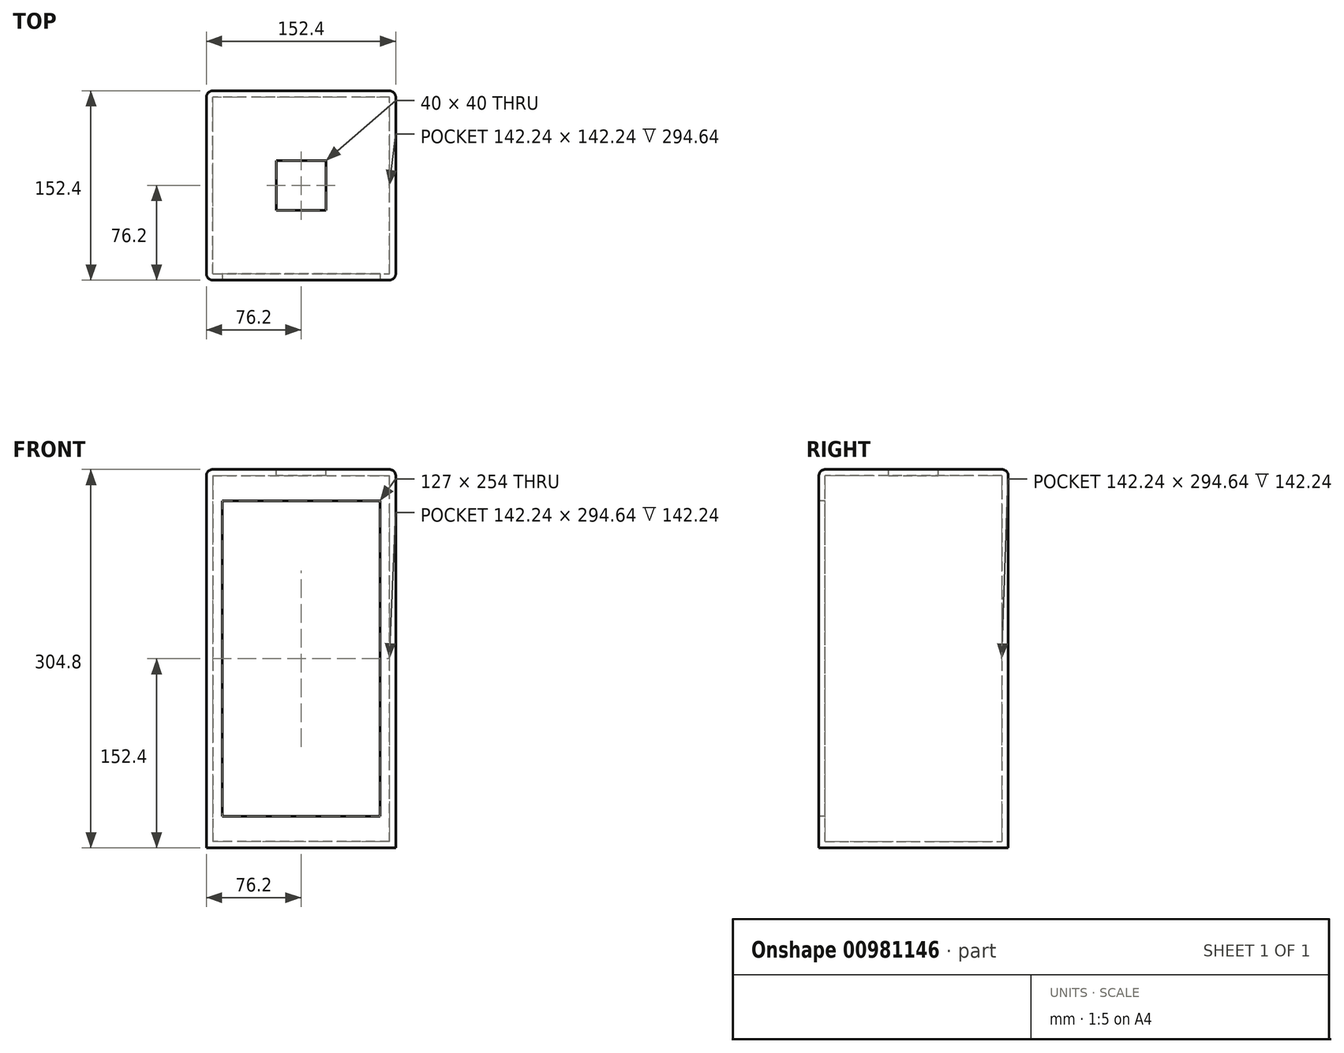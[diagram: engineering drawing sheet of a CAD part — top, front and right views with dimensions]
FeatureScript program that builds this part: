
annotation { "Feature Type Name" : "Feature", "Feature Type Description" : "" }
export const myFeature = defineFeature(function(context is Context, id is Id, definition is map)
    precondition{}
    {
        {
            var Q0;
            Q0=qCreatedBy(makeId("Front.planeOp"),FACE);
            var sketch = newSketch(context, id + "F0", { "sketchPlane" : qUnion([Q0])});
            skLineSegment(sketch, "E0.bottom", {"start": v(76.2, -152.4) * mm, "end": v(-76.2, -152.4) * mm});
            skLineSegment(sketch, "E0.top", {"start": v(76.2, 152.4) * mm, "end": v(-76.2, 152.4) * mm});
            skLineSegment(sketch, "E0.left", {"start": v(76.2, -152.4) * mm, "end": v(76.2, 152.4) * mm});
            skLineSegment(sketch, "E0.right", {"start": v(-76.2, -152.4) * mm, "end": v(-76.2, 152.4) * mm});
            skPoint(sketch, "E0.middle", {"position": v(0, 0) * mm});
            skSolve(sketch);
        }
        {
            var Q0;
            Q0 = qSketchRegion(id + "F0", true);
            extrude(context, id + "F1", {"entities" : qUnion([Q0]), "endBound" : BoundingType.SYMMETRIC, "depth" : 152.4 * mm, "offsetDistance" : 25.4 * mm});
        }
        {
            var Q0;
            Q0=makeQuery(id+"F1.opExtrude","CAP_EDGE",EDGE,{"disambiguationData":[OSD([sQuery(id+"F0.wireOp",EDGE,"E0.top")])],"isStart":false});
            var Q1;
            Q1=makeQuery(id+"F1.opExtrude","SWEPT_EDGE",EDGE,{"disambiguationData":[OSD([sQuery(id+"F0.wireOp",EDGE,"E0.top"),sQuery(id+"F0.wireOp",EDGE,"E0.left")])]});
            var Q2;
            Q2=makeQuery(id+"F1.opExtrude","CAP_EDGE",EDGE,{"disambiguationData":[OSD([sQuery(id+"F0.wireOp",EDGE,"E0.left")])],"isStart":false});
            var Q3;
            Q3=makeQuery(id+"F1.opExtrude","CAP_EDGE",EDGE,{"disambiguationData":[OSD([sQuery(id+"F0.wireOp",EDGE,"E0.left")])],"isStart":true});
            var Q4;
            Q4=makeQuery(id+"F1.opExtrude","CAP_EDGE",EDGE,{"disambiguationData":[OSD([sQuery(id+"F0.wireOp",EDGE,"E0.top")])],"isStart":true});
            var Q5;
            Q5=makeQuery(id+"F1.opExtrude","SWEPT_EDGE",EDGE,{"disambiguationData":[OSD([sQuery(id+"F0.wireOp",EDGE,"E0.top"),sQuery(id+"F0.wireOp",EDGE,"E0.right")])]});
            var Q6;
            Q6=makeQuery(id+"F1.opExtrude","CAP_EDGE",EDGE,{"disambiguationData":[OSD([sQuery(id+"F0.wireOp",EDGE,"E0.right")])],"isStart":false});
            var Q7;
            Q7=makeQuery(id+"F1.opExtrude","CAP_EDGE",EDGE,{"disambiguationData":[OSD([sQuery(id+"F0.wireOp",EDGE,"E0.right")])],"isStart":true});
            fillet(context, id + "F2", {"entities" : qUnion([Q0, Q1, Q2, Q3, Q4, Q5, Q6, Q7]), "radius" : 5.08 * mm, "tangentPropagation" : true, "allowEdgeOverflow" : false});
        }
        {
            var Q0;
            Q0=makeQuery(id+"F1.opExtrude","CAP_FACE",FACE,{"disambiguationData":[OSD([sQuery(id+"F0.wireOp",EDGE,"E0.bottom"),sQuery(id+"F0.wireOp",EDGE,"E0.top"),sQuery(id+"F0.wireOp",EDGE,"E0.left"),sQuery(id+"F0.wireOp",EDGE,"E0.right")])],"isStart":false});
            var Q1;
            Q1=makeQuery(id+"F1.opExtrude","SWEPT_BODY",BODY,{"disambiguationData":[OSD([sQuery(id+"F0.wireOp",EDGE,"E0.bottom"),sQuery(id+"F0.wireOp",EDGE,"E0.top"),sQuery(id+"F0.wireOp",EDGE,"E0.left"),sQuery(id+"F0.wireOp",EDGE,"E0.right")])]});
            shell(context, id + "F3", {"isHollow" : true, "entities" : qUnion([Q0]), "parts" : qUnion([Q1]), "thickness" : 5.08 * mm});
        }
        {
            var Q0;
            Q0=makeQuery(id+"F1.opExtrude","CAP_FACE",FACE,{"disambiguationData":[OSD([sQuery(id+"F0.wireOp",EDGE,"E0.bottom"),sQuery(id+"F0.wireOp",EDGE,"E0.top"),sQuery(id+"F0.wireOp",EDGE,"E0.left"),sQuery(id+"F0.wireOp",EDGE,"E0.right")])],"isStart":false});
            var sketch = newSketch(context, id + "F4", { "sketchPlane" : qUnion([Q0])});
            skLineSegment(sketch, "E1.bottom", {"start": v(63.5, -127) * mm, "end": v(-63.5, -127) * mm});
            skLineSegment(sketch, "E1.top", {"start": v(63.5, 127) * mm, "end": v(-63.5, 127) * mm});
            skLineSegment(sketch, "E1.left", {"start": v(63.5, -127) * mm, "end": v(63.5, 127) * mm});
            skLineSegment(sketch, "E1.right", {"start": v(-63.5, -127) * mm, "end": v(-63.5, 127) * mm});
            skPoint(sketch, "E1.middle", {"position": v(0, 0) * mm});
            skSolve(sketch);
        }
        {
            var Q0;
            Q0 = qSketchRegion(id + "F4", true);
            extrude(context, id + "F5", {"entities" : qUnion([Q0]), "operationType" : NewBodyOperationType.REMOVE, "oppositeDirection" : true, "depth" : 25.4 * mm, "offsetDistance" : 25.4 * mm});
        }
        {
            var Q0;
            Q0=makeQuery(id+"F1.opExtrude","SWEPT_FACE",FACE,{"disambiguationData":[OSD([sQuery(id+"F0.wireOp",EDGE,"E0.top")])]});
            var sketch = newSketch(context, id + "F6", { "sketchPlane" : qUnion([Q0])});
            skLineSegment(sketch, "E2.bottom", {"start": v(20, -20) * mm, "end": v(-20, -20) * mm});
            skLineSegment(sketch, "E2.top", {"start": v(20, 20) * mm, "end": v(-20, 20) * mm});
            skLineSegment(sketch, "E2.left", {"start": v(20, -20) * mm, "end": v(20, 20) * mm});
            skLineSegment(sketch, "E2.right", {"start": v(-20, -20) * mm, "end": v(-20, 20) * mm});
            skPoint(sketch, "E2.middle", {"position": v(0, 0) * mm});
            skSolve(sketch);
        }
        {
            var Q0;
            Q0 = qSketchRegion(id + "F6", true);
            extrude(context, id + "F7", {"entities" : qUnion([Q0]), "operationType" : NewBodyOperationType.REMOVE, "oppositeDirection" : true, "depth" : 5.08 * mm, "offsetDistance" : 25.4 * mm});
        }
    });
